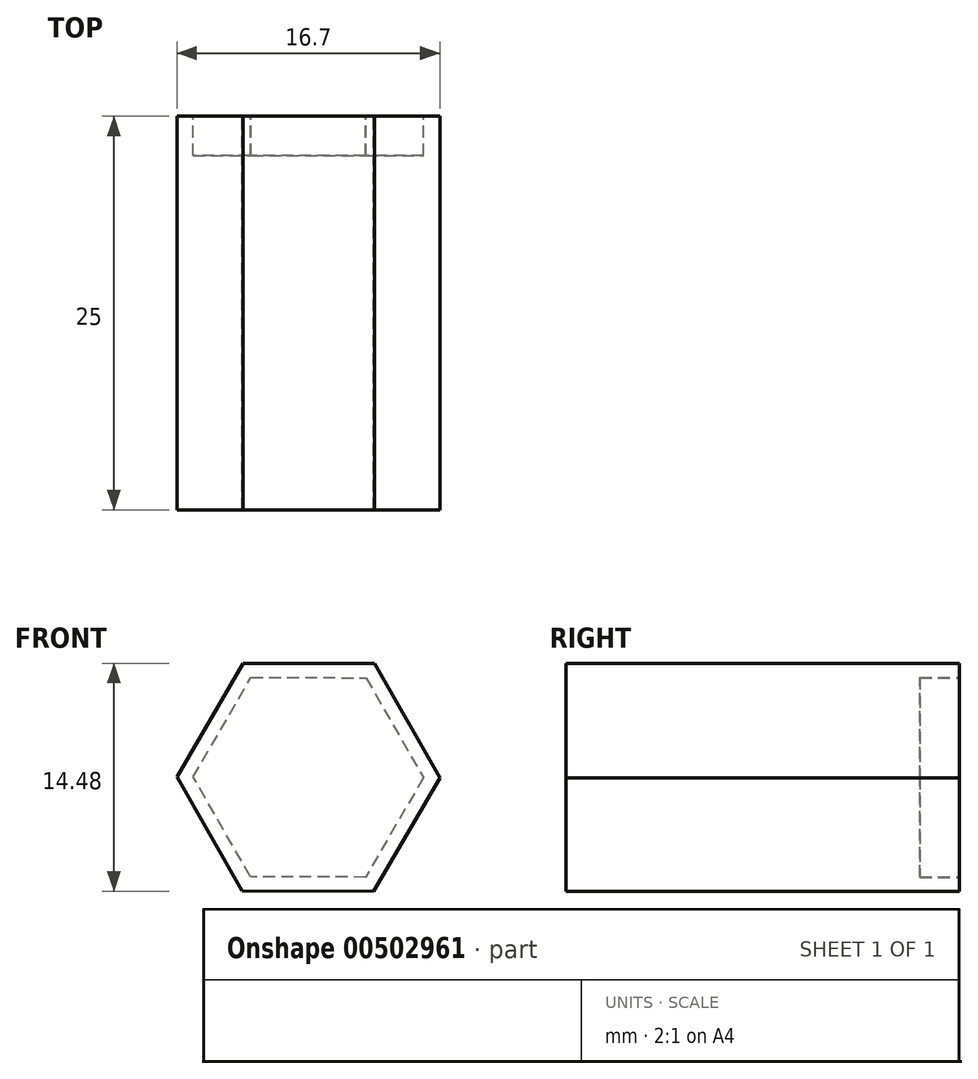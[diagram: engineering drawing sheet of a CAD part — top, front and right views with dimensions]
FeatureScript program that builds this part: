
annotation { "Feature Type Name" : "Feature", "Feature Type Description" : "" }
export const myFeature = defineFeature(function(context is Context, id is Id, definition is map)
    precondition{}
    {
        {
            var Q0;
            Q0=qCreatedBy(makeId("Front.planeOp"),FACE);
            var sketch = newSketch(context, id + "F0", { "sketchPlane" : qUnion([Q0])});
            skCircle(sketch, "E0.cCircle", {"center": v(0, 0) * mm, "radius": 8.35 * mm, "construction": true});
            skLineSegment(sketch, "E0.0", {"start": v(4.2, 7.22) * mm, "end": v(8.35, -0.02) * mm});
            skLineSegment(sketch, "E0.1", {"start": v(8.35, -0.02) * mm, "end": v(4.15, -7.24) * mm});
            skLineSegment(sketch, "E0.2", {"start": v(4.15, -7.24) * mm, "end": v(-4.2, -7.22) * mm});
            skLineSegment(sketch, "E0.3", {"start": v(-4.2, -7.22) * mm, "end": v(-8.35, 0.02) * mm});
            skLineSegment(sketch, "E0.4", {"start": v(-8.35, 0.02) * mm, "end": v(-4.15, 7.24) * mm});
            skLineSegment(sketch, "E0.5", {"start": v(-4.15, 7.24) * mm, "end": v(4.2, 7.22) * mm});
            skSolve(sketch);
        }
        {
            var Q0;
            Q0=makeQuery(id+"F0.imprint","IMPRINT",FACE,{"disambiguationData":[TD([[makeQuery(id+"F0.imprint","IMPRINT",EDGE,{"derivedFrom":sQuery(id+"F0.wireOp",EDGE,"E0.0")}),-1.0]])]});
            extrude(context, id + "F1", {"entities" : qUnion([Q0]), "depth" : 25 * mm, "symmetric" : true});
        }
        {
            var Q0;
            Q0=makeQuery(id+"F1.opExtrude","CAP_FACE",FACE,{"disambiguationData":[OSD([sQuery(id+"F0.wireOp",EDGE,"E0.0"),sQuery(id+"F0.wireOp",EDGE,"E0.1"),sQuery(id+"F0.wireOp",EDGE,"E0.2"),sQuery(id+"F0.wireOp",EDGE,"E0.3"),sQuery(id+"F0.wireOp",EDGE,"E0.4"),sQuery(id+"F0.wireOp",EDGE,"E0.5")])],"isStart":true});
            shell(context, id + "F2", {"entities" : qUnion([Q0]), "thickness" : 0.9 * mm});
        }
        {
            var Q0;
            Q0=makeQuery(id+"F2.opShell","OFFSET_FACE",FACE,{"disambiguationData":[OSD([sQuery(id+"F0.wireOp",EDGE,"E0.0"),sQuery(id+"F0.wireOp",EDGE,"E0.1"),sQuery(id+"F0.wireOp",EDGE,"E0.2"),sQuery(id+"F0.wireOp",EDGE,"E0.3"),sQuery(id+"F0.wireOp",EDGE,"E0.4"),sQuery(id+"F0.wireOp",EDGE,"E0.5")])]});
            extrude(context, id + "F3", {"entities" : qUnion([Q0]), "operationType" : NewBodyOperationType.ADD, "depth" : 21.6 * mm});
        }
    });
